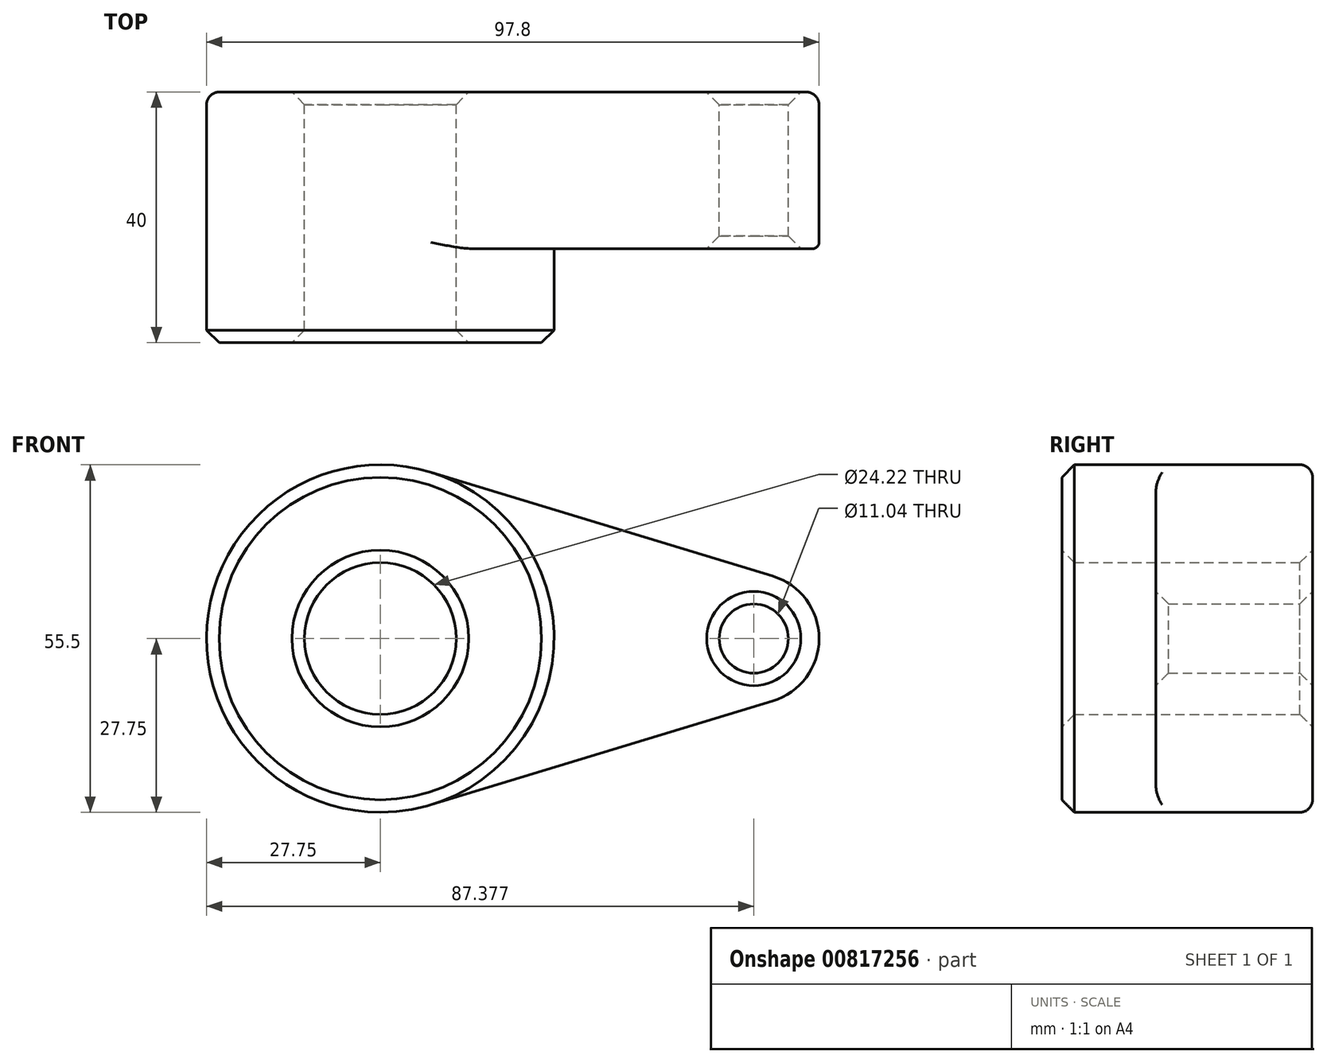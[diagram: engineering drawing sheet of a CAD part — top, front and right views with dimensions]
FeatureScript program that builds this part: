
annotation { "Feature Type Name" : "Feature", "Feature Type Description" : "" }
export const myFeature = defineFeature(function(context is Context, id is Id, definition is map)
    precondition{}
    {
        {
            var Q0;
            Q0=qCreatedBy(makeId("Front.planeOp"),FACE);
            var sketch = newSketch(context, id + "F0", { "sketchPlane" : qUnion([Q0])});
            skCircle(sketch, "E0", {"center": v(0, 0) * mm, "radius": 27.75 * mm});
            skCircle(sketch, "E1", {"center": v(59.63, 0) * mm, "radius": 10.42 * mm});
            skLineSegment(sketch, "E2", {"start": v(8.06, -26.55) * mm, "end": v(62.65, -9.97) * mm});
            skLineSegment(sketch, "E3", {"start": v(8.06, 26.55) * mm, "end": v(62.65, 9.97) * mm});
            skCircle(sketch, "E4", {"center": v(0, 0) * mm, "radius": 12.1 * mm});
            skCircle(sketch, "E5", {"center": v(59.63, 0) * mm, "radius": 5.52 * mm});
            skSolve(sketch);
        }
        {
            var Q0;
            Q0 = qSketchRegion(id + "F0", true);
            extrude(context, id + "F1", {"entities" : qUnion([Q0]), "depth" : 25 * mm, "offsetDistance" : 25 * mm});
        }
        {
            var Q0;
            Q0=makeQuery(id+"F0.imprint","IMPRINT",FACE,{"disambiguationData":[TD([[makeQuery(id+"F0.imprint","IMPRINT",EDGE,{"derivedFrom":sQuery(id+"F0.wireOp",EDGE,"E4")}),-1.0]])]});
            extrude(context, id + "F2", {"entities" : qUnion([Q0]), "operationType" : NewBodyOperationType.ADD, "depth" : 40 * mm, "offsetDistance" : 25 * mm});
        }
        {
            var Q0;
            Q0=makeQuery(id+"F2.opExtrude","CAP_EDGE",EDGE,{"disambiguationData":[OSD([sQuery(id+"F0.wireOp",EDGE,"E4")])],"isStart":false});
            chamfer(context, id + "F3", {"entities" : qUnion([Q0]), "width" : 2 * mm, "tangentPropagation" : true});
        }
        {
            var Q0;
            Q0=makeQuery(id+"F2.opExtrude","CAP_EDGE",EDGE,{"disambiguationData":[OSD([sQuery(id+"F0.wireOp",EDGE,"E0")])],"isStart":false});
            chamfer(context, id + "F4", {"entities" : qUnion([Q0]), "width" : 2 * mm, "tangentPropagation" : true});
        }
        {
            var Q0;
            Q0=makeQuery(id+"F1.opExtrude","CAP_EDGE",EDGE,{"disambiguationData":[OSD([sQuery(id+"F0.wireOp",EDGE,"E5")])],"isStart":false});
            chamfer(context, id + "F5", {"entities" : qUnion([Q0]), "width" : 2 * mm, "tangentPropagation" : true});
        }
        {
            var Q0;
            Q0=makeQuery(id+"F1.opExtrude","CAP_EDGE",EDGE,{"disambiguationData":[OSD([sQuery(id+"F0.wireOp",EDGE,"E4")])],"isStart":true});
            var Q1;
            Q1=makeQuery(id+"F1.opExtrude","CAP_EDGE",EDGE,{"disambiguationData":[OSD([sQuery(id+"F0.wireOp",EDGE,"E5")])],"isStart":true});
            chamfer(context, id + "F6", {"entities" : qUnion([Q0, Q1]), "width" : 2 * mm, "tangentPropagation" : true});
        }
        {
            var Q0;
            Q0=makeQuery(id+"F1.opExtrude","CAP_EDGE",EDGE,{"disambiguationData":[OSD([sQuery(id+"F0.wireOp",EDGE,"E2")])],"isStart":false});
            fillet(context, id + "F7", {"entities" : qUnion([Q0]), "radius" : 1 * mm, "tangentPropagation" : true, "allowEdgeOverflow" : false});
        }
        {
            var Q0;
            Q0=makeQuery(id+"F1.opExtrude","CAP_EDGE",EDGE,{"disambiguationData":[OSD([sQuery(id+"F0.wireOp",EDGE,"E2")])],"isStart":true});
            fillet(context, id + "F8", {"entities" : qUnion([Q0]), "radius" : 2 * mm, "tangentPropagation" : true, "allowEdgeOverflow" : false});
        }
    });
